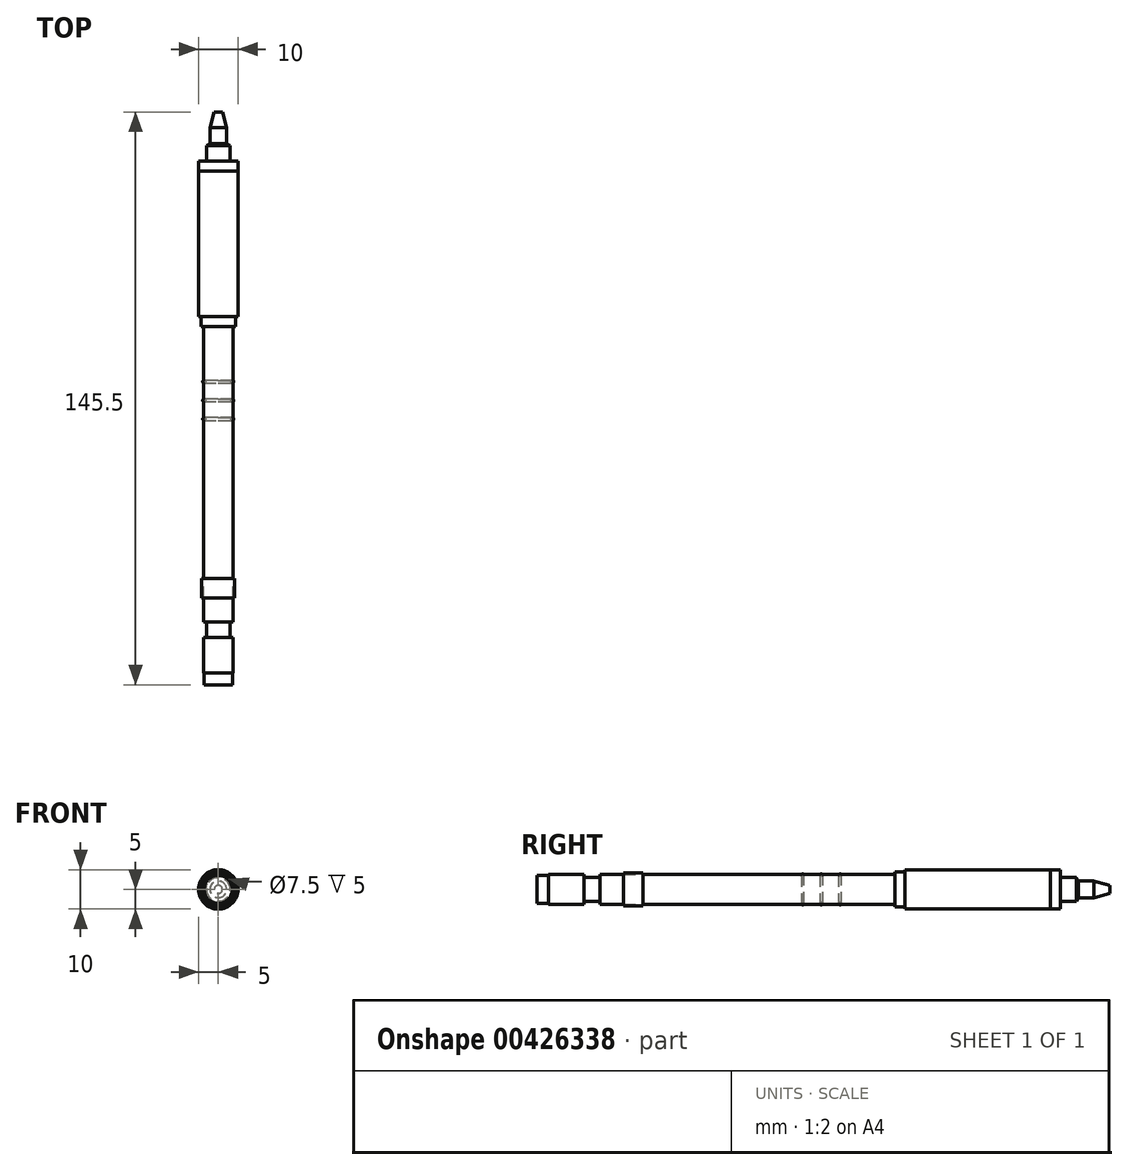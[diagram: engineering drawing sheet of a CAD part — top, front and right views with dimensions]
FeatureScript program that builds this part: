
annotation { "Feature Type Name" : "Feature", "Feature Type Description" : "" }
export const myFeature = defineFeature(function(context is Context, id is Id, definition is map)
    precondition{}
    {
        {
            var Q0;
            Q0=qCreatedBy(makeId("Front.planeOp"),FACE);
            var sketch = newSketch(context, id + "F0", { "sketchPlane" : qUnion([Q0])});
            skCircle(sketch, "E0", {"center": v(0, 0) * mm, "radius": 3.75 * mm});
            skSolve(sketch);
        }
        {
            var Q0;
            Q0 = qSketchRegion(id + "F0", true);
            extrude(context, id + "F1", {"entities" : qUnion([Q0]), "depth" : 75 * mm});
        }
        {
            var Q0;
            Q0=makeQuery(id+"F1.opExtrude","CAP_FACE",FACE,{"disambiguationData":[OSD([sQuery(id+"F0.wireOp",EDGE,"E0")])],"isStart":true});
            var sketch = newSketch(context, id + "F2", { "sketchPlane" : qUnion([Q0])});
            skCircle(sketch, "E1", {"center": v(0, 0) * mm, "radius": 4.4 * mm});
            skSolve(sketch);
        }
        {
            var Q0;
            Q0 = qSketchRegion(id + "F2", true);
            extrude(context, id + "F3", {"entities" : qUnion([Q0]), "operationType" : NewBodyOperationType.ADD, "depth" : 2.5 * mm});
        }
        {
            var Q0;
            Q0=makeQuery(id+"F3.opExtrude","CAP_FACE",FACE,{"disambiguationData":[OSD([sQuery(id+"F2.wireOp",EDGE,"E1")])],"isStart":false});
            var sketch = newSketch(context, id + "F4", { "sketchPlane" : qUnion([Q0])});
            skCircle(sketch, "E2", {"center": v(0, 0) * mm, "radius": 5 * mm});
            skSolve(sketch);
        }
        {
            var Q0;
            Q0 = qSketchRegion(id + "F4", true);
            extrude(context, id + "F5", {"entities" : qUnion([Q0]), "depth" : 37 * mm});
        }
        {
            var Q0;
            Q0=makeQuery(id+"F5.opExtrude","CAP_FACE",FACE,{"disambiguationData":[OSD([sQuery(id+"F4.wireOp",EDGE,"E2")])],"isStart":false});
            var sketch = newSketch(context, id + "F6", { "sketchPlane" : qUnion([Q0])});
            skCircle(sketch, "E3", {"center": v(0, 0) * mm, "radius": 5 * mm});
            skSolve(sketch);
        }
        {
            var Q0;
            Q0 = qSketchRegion(id + "F6", true);
            extrude(context, id + "F7", {"entities" : qUnion([Q0]), "depth" : 2.5 * mm});
        }
        {
            var Q0;
            Q0=makeQuery(id+"F7.opExtrude","CAP_FACE",FACE,{"disambiguationData":[OSD([sQuery(id+"F6.wireOp",EDGE,"E3")])],"isStart":false});
            var sketch = newSketch(context, id + "F8", { "sketchPlane" : qUnion([Q0])});
            skCircle(sketch, "E4", {"center": v(0, 0) * mm, "radius": 3 * mm});
            skSolve(sketch);
        }
        {
            var Q0;
            Q0 = qSketchRegion(id + "F8", true);
            extrude(context, id + "F9", {"entities" : qUnion([Q0]), "operationType" : NewBodyOperationType.ADD, "depth" : 4 * mm});
        }
        {
            var Q0;
            Q0=makeQuery(id+"F9.opExtrude","CAP_FACE",FACE,{"disambiguationData":[OSD([sQuery(id+"F8.wireOp",EDGE,"E4")])],"isStart":false});
            var sketch = newSketch(context, id + "F10", { "sketchPlane" : qUnion([Q0])});
            skCircle(sketch, "E5", {"center": v(0, 0) * mm, "radius": 3 * mm});
            skSolve(sketch);
        }
        {
            var Q0;
            Q0 = qSketchRegion(id + "F10", true);
            extrude(context, id + "F11", {"entities" : qUnion([Q0]), "operationType" : NewBodyOperationType.ADD, "depth" : .5 * mm, "hasDraft" : true, "draftAngle" : 60 * degree, "draftPullDirection" : true});
        }
        {
            var Q0;
            Q0=makeQuery(id+"F11.opExtrude","CAP_FACE",FACE,{"disambiguationData":[OSD([sQuery(id+"F10.wireOp",EDGE,"E5")])],"isStart":false});
            var sketch = newSketch(context, id + "F12", { "sketchPlane" : qUnion([Q0])});
            skCircle(sketch, "E6", {"center": v(0, 0) * mm, "radius": 2.1 * mm});
            skSolve(sketch);
        }
        {
            var Q0;
            Q0 = qSketchRegion(id + "F12", true);
            extrude(context, id + "F13", {"entities" : qUnion([Q0]), "operationType" : NewBodyOperationType.ADD, "depth" : 4 * mm});
        }
        {
            var Q0;
            Q0=makeQuery(id+"F13.opExtrude","CAP_FACE",FACE,{"disambiguationData":[OSD([sQuery(id+"F12.wireOp",EDGE,"E6")])],"isStart":false});
            var sketch = newSketch(context, id + "F14", { "sketchPlane" : qUnion([Q0])});
            skCircle(sketch, "E7", {"center": v(0, 0) * mm, "radius": 2.1 * mm});
            skSolve(sketch);
        }
        {
            var Q0;
            Q0 = qSketchRegion(id + "F14", true);
            extrude(context, id + "F15", {"entities" : qUnion([Q0]), "operationType" : NewBodyOperationType.ADD, "depth" : 4 * mm, "hasDraft" : true, "draftAngle" : 15 * degree, "draftPullDirection" : true});
        }
        {
            var Q0;
            Q0=makeQuery(id+"F1.opExtrude","CAP_FACE",FACE,{"disambiguationData":[OSD([sQuery(id+"F0.wireOp",EDGE,"E0")])],"isStart":false});
            var sketch = newSketch(context, id + "F16", { "sketchPlane" : qUnion([Q0])});
            skCircle(sketch, "E8", {"center": v(0, 0) * mm, "radius": 3 * mm});
            skSolve(sketch);
        }
        {
            var Q0;
            Q0 = qSketchRegion(id + "F16", true);
            extrude(context, id + "F17", {"entities" : qUnion([Q0]), "depth" : 4 * mm});
        }
        {
            var Q0;
            Q0=makeQuery(id+"F17.opExtrude","CAP_FACE",FACE,{"disambiguationData":[OSD([sQuery(id+"F16.wireOp",EDGE,"E8")])],"isStart":false});
            var sketch = newSketch(context, id + "F18", { "sketchPlane" : qUnion([Q0])});
            skCircle(sketch, "E9", {"center": v(0, 0) * mm, "radius": 3.75 * mm});
            skSolve(sketch);
        }
        {
            var Q0;
            Q0 = qSketchRegion(id + "F18", true);
            extrude(context, id + "F19", {"entities" : qUnion([Q0]), "operationType" : NewBodyOperationType.ADD, "depth" : 9 * mm});
        }
        {
            var Q0;
            Q0=makeQuery(id+"F19.opExtrude","CAP_FACE",FACE,{"disambiguationData":[OSD([sQuery(id+"F18.wireOp",EDGE,"E9")])],"isStart":false});
            var sketch = newSketch(context, id + "F20", { "sketchPlane" : qUnion([Q0])});
            skCircle(sketch, "E10", {"center": v(0, 0) * mm, "radius": 3.6 * mm});
            skSolve(sketch);
        }
        {
            var Q0;
            Q0 = qSketchRegion(id + "F20", true);
            extrude(context, id + "F21", {"entities" : qUnion([Q0]), "depth" : 3 * mm});
        }
        {
            var Q0;
            Q0=qCreatedBy(makeId("Top.planeOp"),FACE);
            var sketch = newSketch(context, id + "F22", { "sketchPlane" : qUnion([Q0])});
            skCircle(sketch, "E11", {"center": v(3.6, -14) * mm, "radius": 0.35 * mm});
            skCircle(sketch, "E12.0.1.0", {"center": v(3.6, -18.75) * mm, "radius": 0.35 * mm});
            skCircle(sketch, "E12.0.2.0", {"center": v(3.6, -23.5) * mm, "radius": 0.35 * mm});
            skLineSegment(sketch, "E12.direction1", {"start": v(3.6, -14) * mm, "end": v(28.6, -14) * mm, "construction": true});
            skLineSegment(sketch, "E12.direction2", {"start": v(3.6, -14) * mm, "end": v(3.6, -18.75) * mm, "construction": true});
            skSolve(sketch);
        }
        {
            var Q0;
            Q0 = qSketchRegion(id + "F22", true);
            var Q1;
            Q1=makeQuery(id+"F1.opExtrude","SWEPT_FACE",FACE,{"disambiguationData":[OSD([sQuery(id+"F0.wireOp",EDGE,"E0")])]});
            revolve(context, id + "F23", {"entities" : qUnion([Q0]), "axis" : qUnion([Q1]), "revolveType" : RevolveType.FULL});
        }
        {
            var Q0;
            Q0=makeQuery(id+"F1.opExtrude","CAP_FACE",FACE,{"disambiguationData":[OSD([sQuery(id+"F0.wireOp",EDGE,"E0")])],"isStart":false});
            cPlane(context, id + "F24", {"entities" : qUnion([Q0]), "cplaneType" : CPlaneType.OFFSET, "offset" : 6 * mm, "oppositeDirection" : true, "width" : 150 * mm, "height" : 150 * mm});
        }
        {
            var Q0;
            Q0=qCreatedBy(id+"F24.planeOp",FACE);
            var sketch = newSketch(context, id + "F25", { "sketchPlane" : qUnion([Q0])});
            skCircle(sketch, "E13", {"center": v(0, 0) * mm, "radius": 3.75 * mm});
            skCircle(sketch, "E14", {"center": v(0, 0) * mm, "radius": 4.2 * mm});
            skSolve(sketch);
        }
        {
            var Q0;
            Q0 = qSketchRegion(id + "F25", true);
            extrude(context, id + "F26", {"entities" : qUnion([Q0]), "oppositeDirection" : true, "depth" : 5 * mm});
        }
    });
